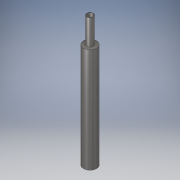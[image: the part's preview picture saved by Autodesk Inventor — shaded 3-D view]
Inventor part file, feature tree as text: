
AUTODESK INVENTOR PART (.ipt)
format: ipt  version: 2018 (Build 220112000, 112)  size: 112,640 bytes
history: native  units: in
note: dims shown in document units (in); Inventor stores cm internally (conversion verified against a paired STEP export)
features: extrude x3, sketch x3
ambient origin geometry x8: Origin, YZ Plane, XZ Plane, XY Plane, X Axis, Y Axis, Z Axis, Center Point
bodies: Solid1 (feature_tree)
feature tree (6):
  extrude  "Extrusion1"  Depth=0.5in
  extrude  "Extrusion2"  Depth=2.0in
  extrude  "Extrusion3"  Depth=8.0in
  sketch  "Sketch1"  dims[d0=0.5in d1=0.025in]
  sketch  "Sketch2"  dims[d2=2.0in d3=0.0in d4=0.95in]
  sketch  "Sketch3"  dims[d5=0.05in d6=0.0in d7=1.0in d8=8.0in d9=0.0in]
